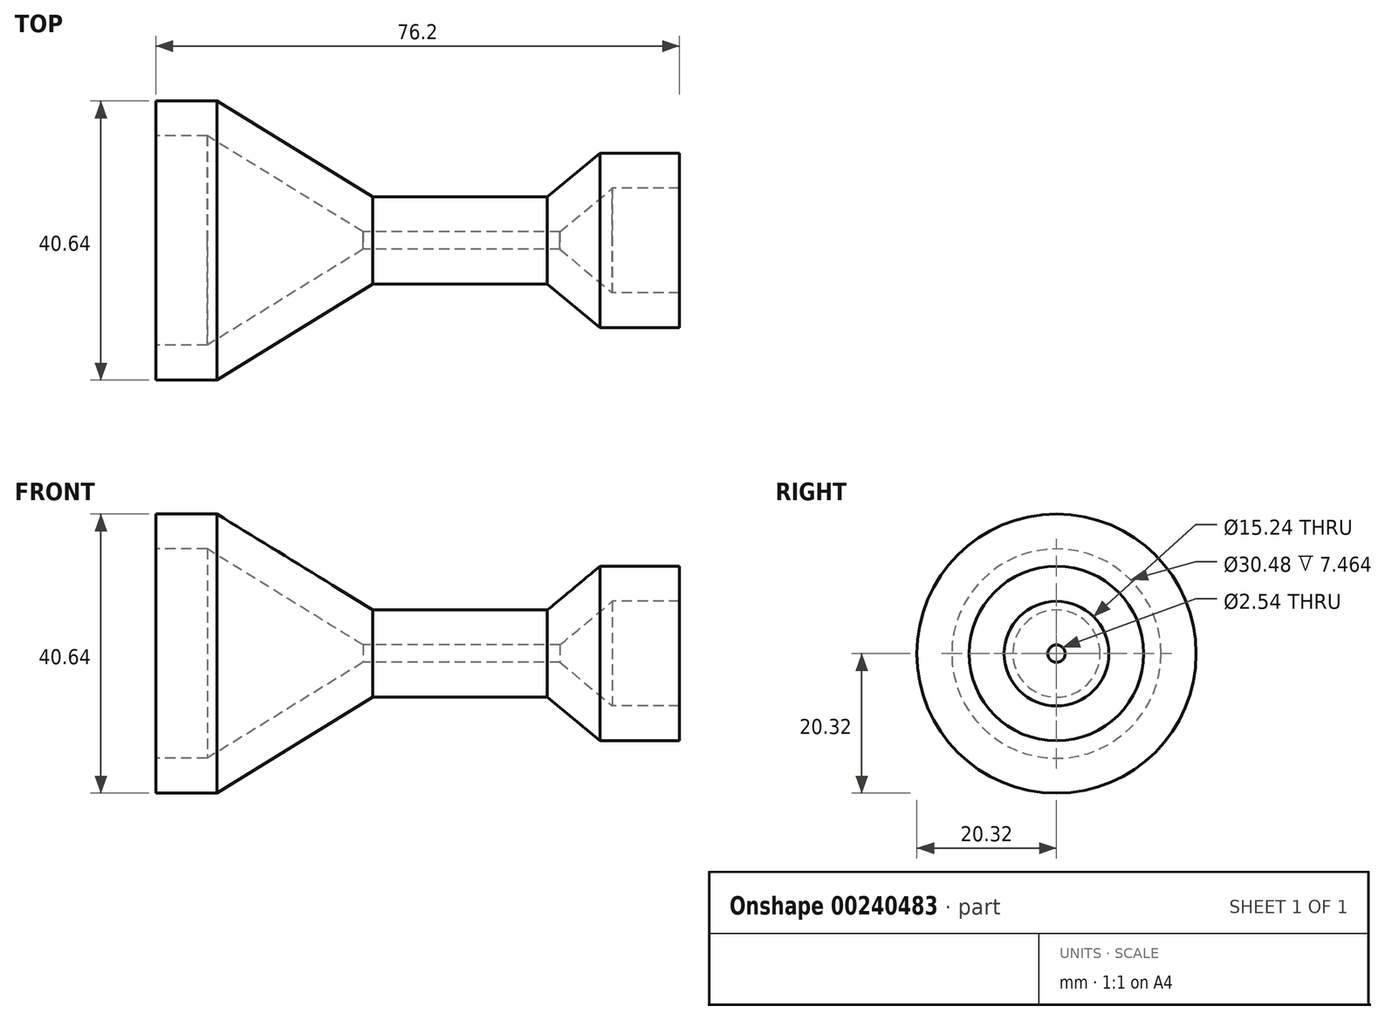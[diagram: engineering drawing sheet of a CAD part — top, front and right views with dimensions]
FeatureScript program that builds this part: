
annotation { "Feature Type Name" : "Feature", "Feature Type Description" : "" }
export const myFeature = defineFeature(function(context is Context, id is Id, definition is map)
    precondition{}
    {
        {
            var Q0;
            Q0=qCreatedBy(makeId("Top.planeOp"),FACE);
            var sketch = newSketch(context, id + "F0", { "sketchPlane" : qUnion([Q0])});
            skLineSegment(sketch, "E0", {"start": v(-192.57, 0) * mm, "end": v(119.14, 0) * mm, "construction": true});
            skLineSegment(sketch, "E1", {"start": v(-67.64, 7.62) * mm, "end": v(-67.64, 12.7) * mm});
            skLineSegment(sketch, "E2", {"start": v(-67.64, 12.7) * mm, "end": v(-79.23, 12.7) * mm});
            skLineSegment(sketch, "E3", {"start": v(-79.23, 12.7) * mm, "end": v(-86.86, 6.35) * mm});
            skLineSegment(sketch, "E4", {"start": v(-86.86, 6.35) * mm, "end": v(-112.26, 6.35) * mm});
            skLineSegment(sketch, "E5", {"start": v(-112.26, 6.35) * mm, "end": v(-134.93, 20.32) * mm});
            skLineSegment(sketch, "E6", {"start": v(-134.93, 20.32) * mm, "end": v(-143.84, 20.32) * mm});
            skLineSegment(sketch, "E7", {"start": v(-143.84, 20.32) * mm, "end": v(-143.84, 15.24) * mm});
            skLineSegment(sketch, "E8.0", {"start": v(-136.37, 15.24) * mm, "end": v(-143.84, 15.24) * mm});
            skLineSegment(sketch, "E8.1", {"start": v(-67.64, 7.62) * mm, "end": v(-77.4, 7.62) * mm});
            skLineSegment(sketch, "E8.2", {"start": v(-77.4, 7.62) * mm, "end": v(-85.02, 1.27) * mm});
            skLineSegment(sketch, "E8.3", {"start": v(-85.02, 1.27) * mm, "end": v(-113.7, 1.27) * mm});
            skLineSegment(sketch, "E8.4", {"start": v(-113.7, 1.27) * mm, "end": v(-136.37, 15.24) * mm});
            skSolve(sketch);
        }
        {
            var Q0;
            Q0 = qSketchRegion(id + "F0", true);
            var Q1;
            Q1=sQuery(id+"F0.wireOp",EDGE,"E0");
            revolve(context, id + "F1", {"entities" : qUnion([Q0]), "axis" : qUnion([Q1]), "revolveType" : RevolveType.FULL});
        }
    });
